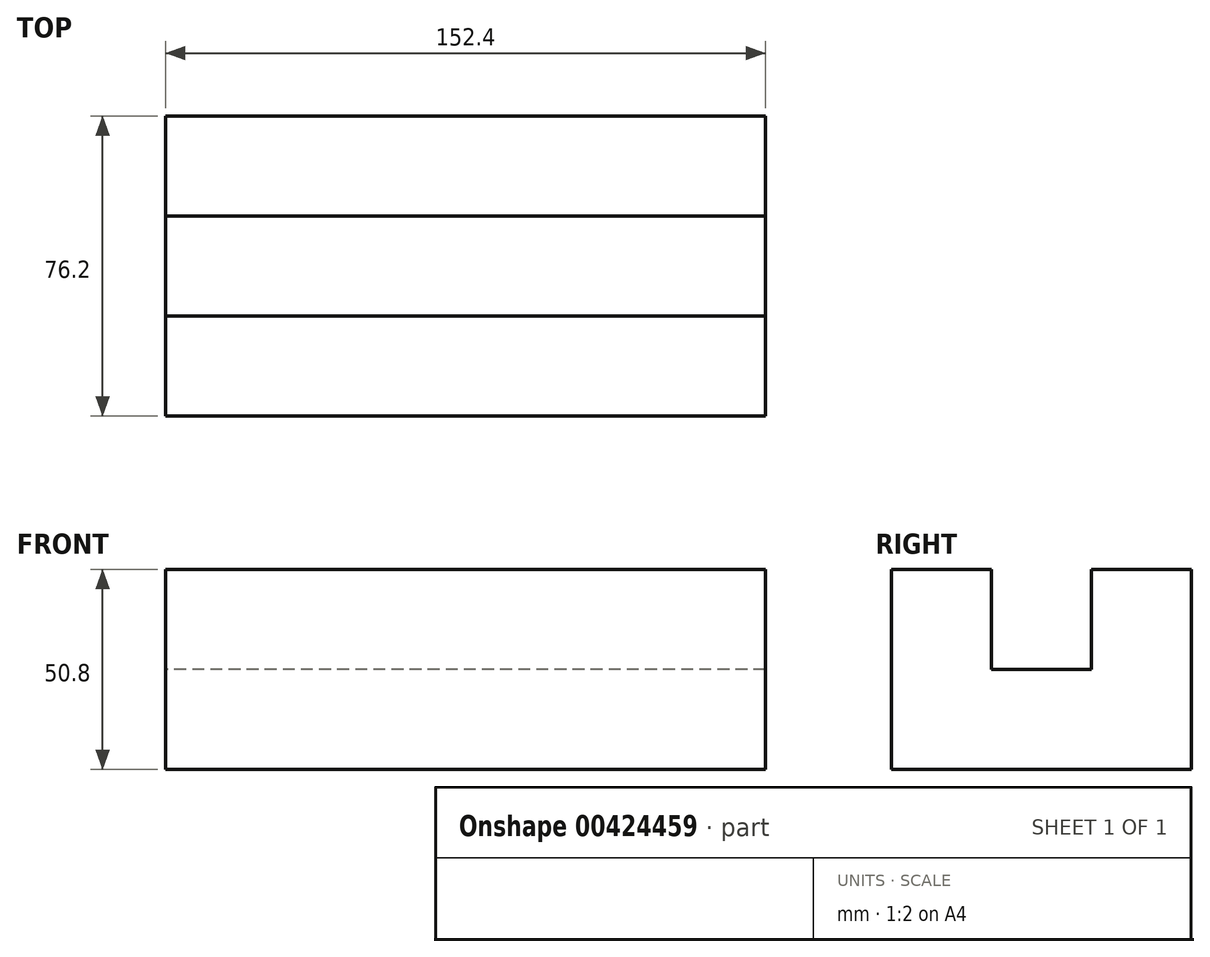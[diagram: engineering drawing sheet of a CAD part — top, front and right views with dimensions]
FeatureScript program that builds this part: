
annotation { "Feature Type Name" : "Feature", "Feature Type Description" : "" }
export const myFeature = defineFeature(function(context is Context, id is Id, definition is map)
    precondition{}
    {
        {
            var Q0;
            Q0=qCreatedBy(makeId("Right.planeOp"),FACE);
            var sketch = newSketch(context, id + "F0", { "sketchPlane" : qUnion([Q0])});
            skLineSegment(sketch, "E0", {"start": v(0, 0) * mm, "end": v(0, 50.8) * mm});
            skLineSegment(sketch, "E1", {"start": v(0, 50.8) * mm, "end": v(25.4, 50.8) * mm});
            skLineSegment(sketch, "E2", {"start": v(25.4, 50.8) * mm, "end": v(25.4, 25.4) * mm});
            skLineSegment(sketch, "E3", {"start": v(50.8, 25.4) * mm, "end": v(25.4, 25.4) * mm});
            skLineSegment(sketch, "E4", {"start": v(50.8, 25.4) * mm, "end": v(50.8, 50.8) * mm});
            skLineSegment(sketch, "E5", {"start": v(50.8, 50.8) * mm, "end": v(76.2, 50.8) * mm});
            skLineSegment(sketch, "E6", {"start": v(76.2, 50.8) * mm, "end": v(76.2, 0) * mm});
            skLineSegment(sketch, "E7", {"start": v(76.2, 0) * mm, "end": v(0, 0) * mm});
            skSolve(sketch);
        }
        {
            var Q0;
            Q0=makeQuery(id+"F0.imprint","IMPRINT",FACE,{"disambiguationData":[TD([[makeQuery(id+"F0.imprint","IMPRINT",EDGE,{"derivedFrom":sQuery(id+"F0.wireOp",EDGE,"E0")}),-1.0]])]});
            extrude(context, id + "F1", {"entities" : qUnion([Q0]), "depth" : 152.4 * mm});
        }
    });
